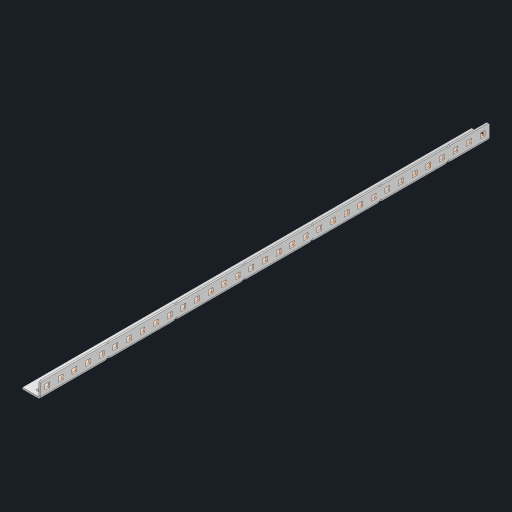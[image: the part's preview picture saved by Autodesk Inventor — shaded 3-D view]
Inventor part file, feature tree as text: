
AUTODESK INVENTOR PART (.ipt)
format: ipt  version: 2023 (Build 270158000, 158)  size: 1,026,048 bytes
history: native  units: in
note: dims shown in document units (in); Inventor stores cm internally (conversion verified against a paired STEP export)
features: other x71, extrude x65, sheet_metal_op x10, sketch x8, mirror x1, pattern_linear x1, chamfer x1
ambient origin geometry x8: Origin, YZ Plane, XZ Plane, XY Plane, X Axis, Y Axis, Z Axis, Center Point
bodies: Solid1 (feature_tree), Body (feature_tree)
feature tree (157):
  other  "Flange Pattern Plane"
  sheet_metal_op  "Flange Pattern"
  sheet_metal_op  "Body Pattern"
  other  "Arc Length"
  mirror  "Notch Mirror"
  pattern_linear  "Notch Pattern"  Spacing1=0.25in  [1 undecoded]
  chamfer  "End Chamfer"
  extrude  "Half Cut"  Depth=0.0625in
  sketch  "Sketch1"  dims[d0=1.5in]
  other  "Plate1"
  sketch  "Sketch2"  dims[d1=16.5in]
  other  "Plate2"
  sheet_metal_op  "Bend1"
  sheet_metal_op  "Corner1"
  sketch  "Sketch3"  dims[d2=0.0625in]
  other  "Flange Pattern Sketch"
  sketch  "Sketch7"  dims[d3=0.0625in]
  other  "Srf1"
  other  "Srf2"
  sketch  "Sketch8"  dims[d4=0.0312in]
  sketch  "Sketch9"  dims[d5=0.125in]
  other  "Srf91"
  sheet_metal_op  "Body Pattern Sketch"
  other  "Srf92"
  sketch  "Sketch13"  dims[d6=0.0625in]
  sketch  "Sketch14"  dims[d7=0.5in d8=90.0deg d9=0.0312in d10=0.25in d11=0.0625in d12=0.0625in d16=0.182in d17=0.02in d18=0.0625in d19=0.0in d20=0.25in d21=0.25in d46=0.172in d47=1.0in d48=0.0in d49=0.182in d50=0.02in d51=0.25in d52=0.25in d53=0.0625in d54=0.0in d55=0.172in d56=1.0in d57=0.0in d60=12.9921in d62=0.5in d63=0.3937in d65=0.5in d85=0.1473in d86=0.1782in d88=0.04in d89=0.0625in d90=0.0in d91=0.04in d92=0.0491in d95=2.5in d96=0.04in d97=0.25in d98=45.0deg d101=0.0in d102=2.497in d131=0.5in d132=12.9921in d134=0.5in d139=0.5in]
  other  "Srf856"
  other  "Srf1310"
  other  "Srf1311"
  other  "Srf1312"
  other  "Srf1376"
  other  "Srf1377"
  other  "Srf1728"
  other  "Srf1755"
  other  "Srf1878"
  other  "Srf1879"
  other  "Srf1880"
  other  "Srf1881"
  other  "Srf1882"
  other  "Srf1883"
  other  "Srf1884"
  other  "Srf1885"
  other  "Srf1886"
  other  "Srf1887"
  other  "Srf1888"
  other  "Srf1889"
  other  "Srf1890"
  other  "Srf1891"
  other  "Srf1892"
  other  "Srf1893"
  other  "Srf1894"
  other  "Srf1895"
  other  "Srf1896"
  other  "Srf1897"
  other  "Srf1898"
  other  "Srf1899"
  other  "Srf1900"
  other  "Srf1901"
  other  "Srf1902"
  other  "Srf1903"
  other  "Srf1904"
  other  "Srf1942"
  other  "Srf1943"
  other  "Srf1944"
  other  "Srf1945"
  other  "Srf1946"
  other  "Srf1947"
  other  "Srf1948"
  other  "Srf1949"
  other  "Srf1950"
  other  "Srf1951"
  other  "Srf1952"
  other  "Srf1953"
  other  "Srf1954"
  other  "Srf1955"
  other  "Srf1956"
  other  "Srf1957"
  other  "Srf1958"
  other  "Srf1959"
  other  "Srf1960"
  other  "Srf1961"
  other  "Srf1962"
  other  "Srf1963"
  other  "Srf1964"
  other  "Srf1965"
  other  "Srf1966"
  other  "Srf1967"
  other  "Srf1968"
  sheet_metal_op  "Flange Stamp"
  sheet_metal_op  "Flange Circle"
  sheet_metal_op  "Body Stamp"
  sheet_metal_op  "Body Circle"
  sheet_metal_op  "Notch"
  extrude  "ExtrusionSrf2"  Depth=0.0625in
  extrude  "ExtrusionSrf92"  Depth=0.5in
  extrude  "ExtrusionSrf856"  Depth=0.02in
  extrude  "ExtrusionSrf1310"  Depth=0.0625in
  extrude  "ExtrusionSrf1311"  TaperAngle=0.0deg  [1 undecoded]
  extrude  "ExtrusionSrf1312"  Depth=0.5in
  extrude  "ExtrusionSrf1376"  Depth=0.5in
  extrude  "ExtrusionSrf1377"  Depth=0.5in
  extrude  "ExtrusionSrf1728"  Depth=0.5in TaperAngle=0.0deg
  extrude  "ExtrusionSrf1755"  Depth=0.5in
  extrude  "ExtrusionSrf1878"  Depth=0.02in
  extrude  "ExtrusionSrf1879"  Depth=0.5in
  extrude  "ExtrusionSrf1880"  Depth=0.5in
  extrude  "ExtrusionSrf1881"  Depth=0.0625in
  extrude  "ExtrusionSrf1882"  TaperAngle=0.0deg  [1 undecoded]
  extrude  "ExtrusionSrf1883"  Depth=0.5in
  extrude  "ExtrusionSrf1884"  Depth=0.5in TaperAngle=0.0deg
  extrude  "ExtrusionSrf1885"  Depth=0.5in
  extrude  "ExtrusionSrf1886"  Depth=0.5in
  extrude  "ExtrusionSrf1887"  Depth=0.5in
  extrude  "ExtrusionSrf1888"  Depth=0.5in
  extrude  "ExtrusionSrf1889"  Depth=0.5in
  extrude  "ExtrusionSrf1890"  Depth=0.0625in
  extrude  "ExtrusionSrf1891"  TaperAngle=0.0deg  [1 undecoded]
  extrude  "ExtrusionSrf1892"  Depth=0.5in
  extrude  "ExtrusionSrf1893"  Depth=0.5in
  extrude  "ExtrusionSrf1894"  Depth=0.5in
  extrude  "ExtrusionSrf1895"  Depth=0.5in TaperAngle=45.0deg
  extrude  "ExtrusionSrf1896"  TaperAngle=0.0deg  [1 undecoded]
  extrude  "ExtrusionSrf1897"  Depth=0.5in
  extrude  "ExtrusionSrf1898"  Depth=0.5in
  extrude  "ExtrusionSrf1899"  Depth=0.5in
  extrude  "ExtrusionSrf1900"  Depth=0.5in
  extrude  "ExtrusionSrf1901"  Depth=0.5in
  extrude  "ExtrusionSrf1902"  [1 undecoded]
  extrude  "ExtrusionSrf1903"  [1 undecoded]
  extrude  "ExtrusionSrf1904"  [1 undecoded]
  extrude  "ExtrusionSrf1942"  [1 undecoded]
  extrude  "ExtrusionSrf1943"  [1 undecoded]
  extrude  "ExtrusionSrf1944"  [1 undecoded]
  extrude  "ExtrusionSrf1945"  [1 undecoded]
  extrude  "ExtrusionSrf1946"  [1 undecoded]
  extrude  "ExtrusionSrf1947"  [1 undecoded]
  extrude  "ExtrusionSrf1948"  [1 undecoded]
  extrude  "ExtrusionSrf1949"  [1 undecoded]
  extrude  "ExtrusionSrf1950"  [1 undecoded]
  extrude  "ExtrusionSrf1951"  [1 undecoded]
  extrude  "ExtrusionSrf1952"  [1 undecoded]
  extrude  "ExtrusionSrf1953"  [1 undecoded]
  extrude  "ExtrusionSrf1954"  [1 undecoded]
  extrude  "ExtrusionSrf1955"  [1 undecoded]
  extrude  "ExtrusionSrf1956"  [1 undecoded]
  extrude  "ExtrusionSrf1957"  [1 undecoded]
  extrude  "ExtrusionSrf1958"  [1 undecoded]
  extrude  "ExtrusionSrf1959"  [1 undecoded]
  extrude  "ExtrusionSrf1960"  [1 undecoded]
  extrude  "ExtrusionSrf1961"  [1 undecoded]
  extrude  "ExtrusionSrf1962"  [1 undecoded]
  extrude  "ExtrusionSrf1963"  [1 undecoded]
  extrude  "ExtrusionSrf1964"  [1 undecoded]
  extrude  "ExtrusionSrf1965"  [1 undecoded]
  extrude  "ExtrusionSrf1966"  [1 undecoded]
  extrude  "ExtrusionSrf1967"  [1 undecoded]
  extrude  "ExtrusionSrf1968"  [1 undecoded]
note: 35 required parameter values undecoded (feature->parameter linkage not recoverable at this tier; creation-order binding heuristic only, values carry confidence <= 0.55)
